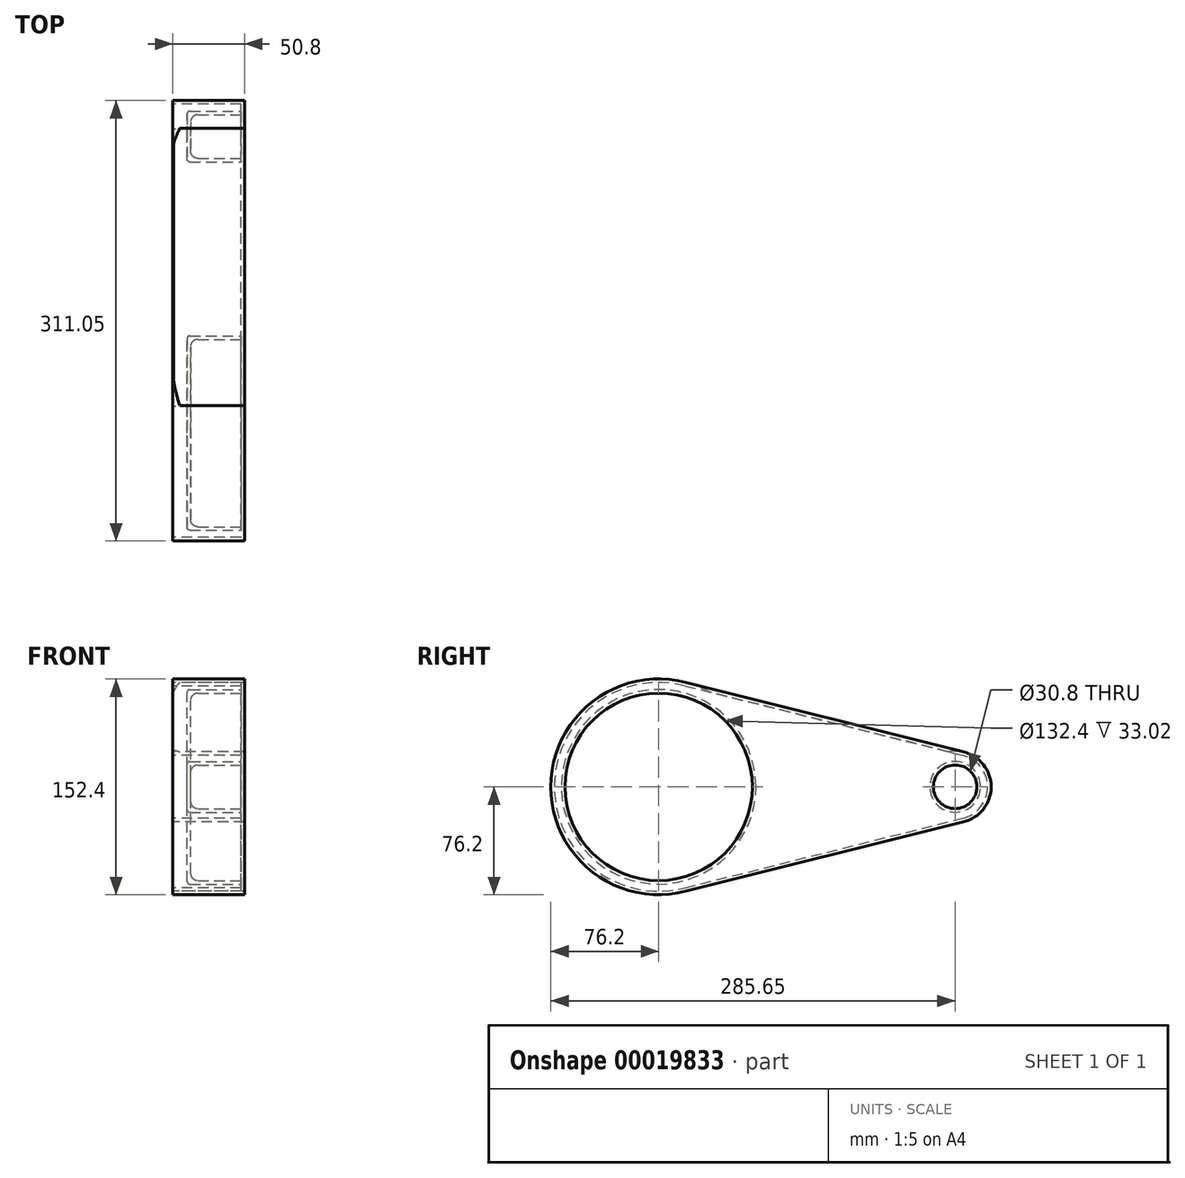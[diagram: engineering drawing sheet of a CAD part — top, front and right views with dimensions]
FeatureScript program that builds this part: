
annotation { "Feature Type Name" : "Feature", "Feature Type Description" : "" }
export const myFeature = defineFeature(function(context is Context, id is Id, definition is map)
    precondition{}
    {
        {
            var Q0;
            Q0=qCreatedBy(makeId("Right.planeOp"),FACE);
            var sketch = newSketch(context, id + "F0", { "sketchPlane" : qUnion([Q0])});
            skCircle(sketch, "E0", {"center": v(0, 0) * mm, "radius": 76.2 * mm});
            skCircle(sketch, "E1", {"center": v(209.45, 0) * mm, "radius": 25.4 * mm});
            skLineSegment(sketch, "E2", {"start": v(18.48, 73.92) * mm, "end": v(215.61, 24.64) * mm});
            skLineSegment(sketch, "E3", {"start": v(18.48, -73.92) * mm, "end": v(215.61, -24.64) * mm});
            skSolve(sketch);
        }
        {
            var Q0;
            {var subQ0=sQuery(id+"F0.wireOp",EDGE,"E0");var subQ2=makeQuery(id+"F0.imprint","INTERSECT",VERTEX,{"derivedFrom":[subQ0,sQuery(id+"F0.wireOp",EDGE,"E2")]});Q0=makeQuery(id+"F0.imprint","IMPRINT",FACE,{"disambiguationData":[TD([[makeQuery(id+"F0.imprint","IMPRINT",EDGE,{"disambiguationData":[TD([[subQ2,-1.0]])],"derivedFrom":subQ0}),1.0]])]});}
            var Q1;
            {var subQ1=sQuery(id+"F0.wireOp",EDGE,"E2");Q1=makeQuery(id+"F0.imprint","IMPRINT",FACE,{"disambiguationData":[TD([[makeQuery(id+"F0.imprint","IMPRINT",EDGE,{"derivedFrom":subQ1}),-1.0]])]});}
            var Q2;
            {var subQ0=sQuery(id+"F0.wireOp",EDGE,"E1");var subQ2=makeQuery(id+"F0.imprint","INTERSECT",VERTEX,{"derivedFrom":[subQ0,sQuery(id+"F0.wireOp",EDGE,"E2")]});Q2=makeQuery(id+"F0.imprint","IMPRINT",FACE,{"disambiguationData":[TD([[makeQuery(id+"F0.imprint","IMPRINT",EDGE,{"disambiguationData":[TD([[subQ2,-1.0]])],"derivedFrom":subQ0}),1.0]])]});}
            extrude(context, id + "F1", {"entities" : qUnion([Q0, Q1, Q2]), "depth" : 50.8 * mm});
        }
        {
            var Q0;
            Q0=makeQuery(id+"F1.opExtrude","CAP_FACE",FACE,{"disambiguationData":[OSD([sQuery(id+"F0.wireOp",EDGE,"E0"),sQuery(id+"F0.wireOp",EDGE,"E1"),sQuery(id+"F0.wireOp",EDGE,"E2"),sQuery(id+"F0.wireOp",EDGE,"E3")])],"isStart":false});
            var sketch = newSketch(context, id + "F2", { "sketchPlane" : qUnion([Q0])});
            skCircle(sketch, "E4", {"center": v(0, 0) * mm, "radius": 66.2 * mm});
            skCircle(sketch, "E5", {"center": v(209.45, 0) * mm, "radius": 15.4 * mm});
            skSolve(sketch);
        }
        {
            var Q0;
            Q0 = qSketchRegion(id + "F2", true);
            extrude(context, id + "F3", {"entities" : qUnion([Q0]), "operationType" : NewBodyOperationType.REMOVE, "oppositeDirection" : true, "depth" : 38.1 * mm});
        }
        {
            var Q0;
            Q0=makeQuery(id+"F1.opExtrude","CAP_FACE",FACE,{"disambiguationData":[OSD([sQuery(id+"F0.wireOp",EDGE,"E0"),sQuery(id+"F0.wireOp",EDGE,"E1"),sQuery(id+"F0.wireOp",EDGE,"E2"),sQuery(id+"F0.wireOp",EDGE,"E3")])],"isStart":true});
            shell(context, id + "F4", {"entities" : qUnion([Q0]), "thickness" : 2.5 * mm});
        }
        {
            var Q0;
            Q0=makeQuery(id+"F1.opExtrude","CAP_EDGE",EDGE,{"disambiguationData":[OSD([sQuery(id+"F0.wireOp",EDGE,"E2")])],"isStart":true});
            var Q1;
            Q1=makeQuery(id+"F3.boolean.opBoolean","COPY",EDGE,{"derivedFrom":makeQuery(id+"F3.opExtrude","CAP_EDGE",EDGE,{"disambiguationData":[OSD([sQuery(id+"F2.wireOp",EDGE,"E4")])],"isStart":false})});
            var Q2;
            Q2=makeQuery(id+"F3.boolean.opBoolean","COPY",EDGE,{"derivedFrom":makeQuery(id+"F3.opExtrude","CAP_EDGE",EDGE,{"disambiguationData":[OSD([sQuery(id+"F2.wireOp",EDGE,"E5")])],"isStart":false})});
            fillet(context, id + "F5", {"entities" : qUnion([Q0, Q1, Q2]), "radius" : 5.08 * mm, "tangentPropagation" : true, "allowEdgeOverflow" : false});
        }
        {
            var Q0;
            {var subQ0=sQuery(id+"F2.wireOp",EDGE,"E4");Q0=makeQuery(id+"F4.opShell","OFFSET_EDGE",EDGE,{"disambiguationData":[OSD([subQ0]),TDD([makeQuery(id+"F3.boolean.opBoolean","COPY",EDGE,{"derivedFrom":makeQuery(id+"F3.opExtrude","CAP_EDGE",EDGE,{"disambiguationData":[OSD([subQ0])],"isStart":false})})])]});}
            fillet(context, id + "F6", {"entities" : qUnion([Q0]), "radius" : 2 * mm, "tangentPropagation" : true, "allowEdgeOverflow" : false});
        }
        {
            var Q0;
            {var subQ0=sQuery(id+"F2.wireOp",EDGE,"E5");Q0=makeQuery(id+"F4.opShell","OFFSET_EDGE",EDGE,{"disambiguationData":[OSD([subQ0]),TDD([makeQuery(id+"F3.boolean.opBoolean","COPY",EDGE,{"derivedFrom":makeQuery(id+"F3.opExtrude","CAP_EDGE",EDGE,{"disambiguationData":[OSD([subQ0])],"isStart":false})})])]});}
            fillet(context, id + "F7", {"entities" : qUnion([Q0]), "radius" : 2 * mm, "tangentPropagation" : true, "allowEdgeOverflow" : false});
        }
    });
